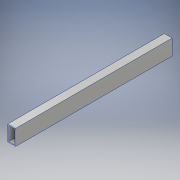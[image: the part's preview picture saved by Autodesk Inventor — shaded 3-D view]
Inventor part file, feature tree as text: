
AUTODESK INVENTOR PART (.ipt)
format: ipt  version: 2016 (Build 200138000, 138)  size: 108,544 bytes
history: native  units: in
note: dims shown in document units (in); Inventor stores cm internally (conversion verified against a paired STEP export)
features: extrude x1, sketch x1
ambient origin geometry x8: Origin, YZ Plane, XZ Plane, XY Plane, X Axis, Y Axis, Z Axis, Center Point
bodies: Solid1 (feature_tree)
feature tree (2):
  extrude  "Extrusion1"  Depth=2.0in
  sketch  "Sketch1"  dims[d0=1.0in d1=2.0in d2=0.125in d3=20.0in d4=0.0in]
